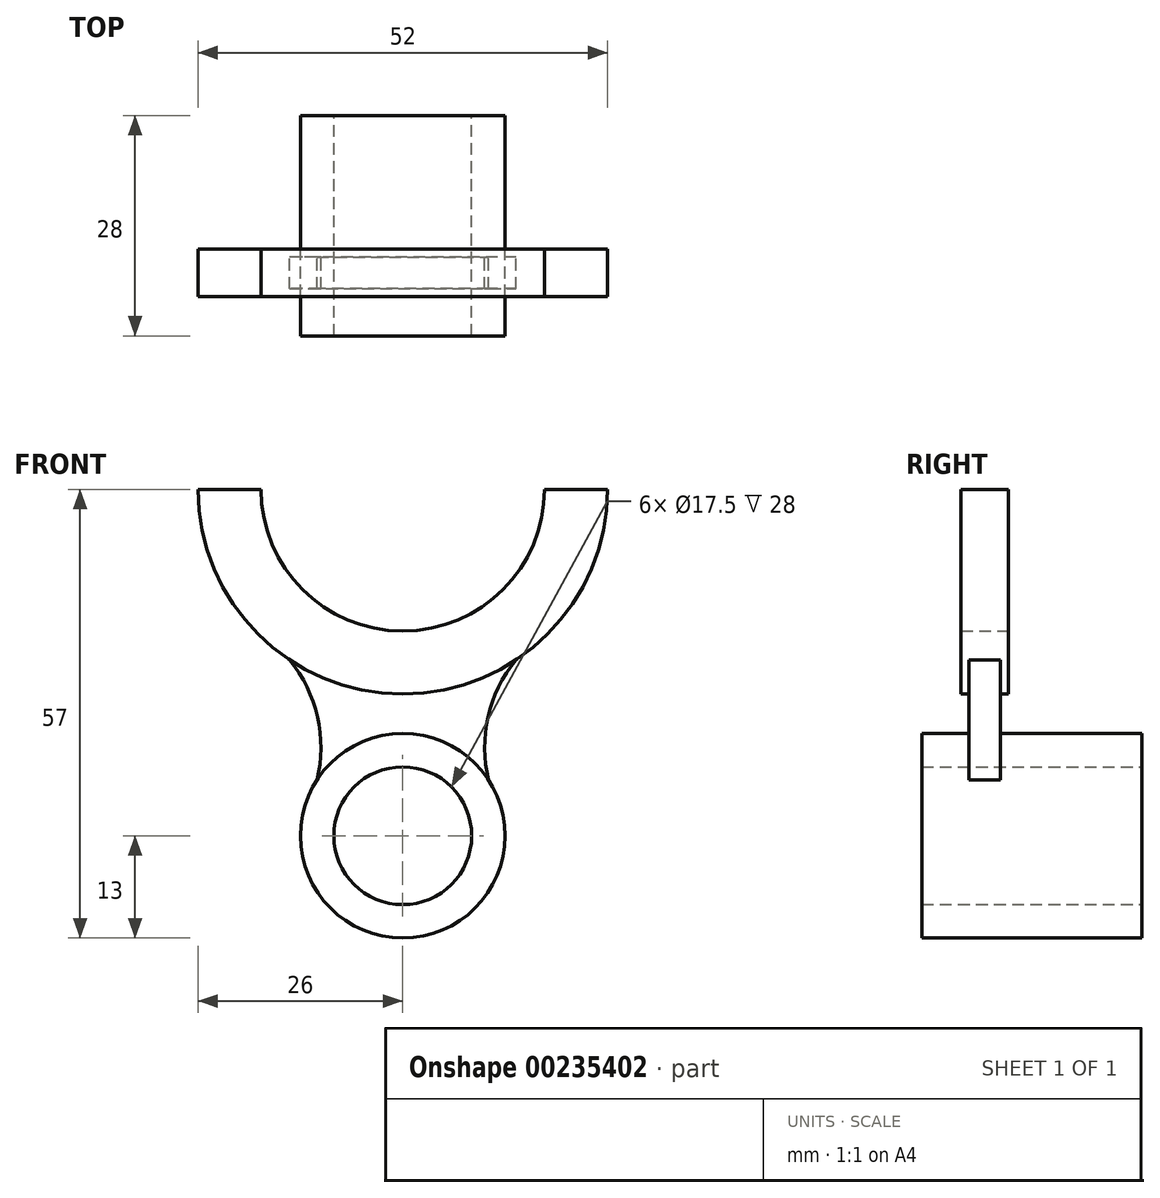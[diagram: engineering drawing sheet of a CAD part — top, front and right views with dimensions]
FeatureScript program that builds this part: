
annotation { "Feature Type Name" : "Feature", "Feature Type Description" : "" }
export const myFeature = defineFeature(function(context is Context, id is Id, definition is map)
    precondition{}
    {
        {
            var Q0;
            Q0=qCreatedBy(makeId("Front.planeOp"),FACE);
            var sketch = newSketch(context, id + "F0", { "sketchPlane" : qUnion([Q0])});
            skCircle(sketch, "E0", {"center": v(0, 0) * mm, "radius": 8.75 * mm});
            skCircle(sketch, "E1", {"center": v(0, 0) * mm, "radius": 13 * mm});
            skArc(sketch, "E2", {"start": v(12.76, 2.47) * mm, "mid": v(10.99, 15.74) * mm, "end": v(19.12, 26.38) * mm});
            skArc(sketch, "E3.MirrorCS", {"start": v(-12.76, 2.47) * mm, "mid": v(-10.99, 15.74) * mm, "end": v(-19.12, 26.38) * mm});
            skArc(sketch, "E4", {"start": v(-26, 44) * mm, "mid": v(0, 18) * mm, "end": v(26, 44) * mm});
            skLineSegment(sketch, "E5", {"start": v(-26, 44) * mm, "end": v(-18, 44) * mm});
            skArc(sketch, "E6", {"start": v(-18, 44) * mm, "mid": v(0, 26) * mm, "end": v(18, 44) * mm});
            skLineSegment(sketch, "E7", {"start": v(18, 44) * mm, "end": v(26, 44) * mm});
            skSolve(sketch);
        }
        {
            var Q0;
            Q0 = qSketchRegion(id + "F0", true);
            extrude(context, id + "F1", {"entities" : qUnion([Q0]), "depth" : 28 * mm});
        }
        {
            var Q0;
            Q0=makeQuery(id+"F1.opExtrude","CAP_FACE",FACE,{"disambiguationData":[OSD([sQuery(id+"F0.wireOp",EDGE,"E2"),sQuery(id+"F0.wireOp",EDGE,"E3.MirrorCS"),sQuery(id+"F0.wireOp",EDGE,"E1"),sQuery(id+"F0.wireOp",EDGE,"E0"),sQuery(id+"F0.wireOp",EDGE,"E4"),sQuery(id+"F0.wireOp",EDGE,"E5"),sQuery(id+"F0.wireOp",EDGE,"E6"),sQuery(id+"F0.wireOp",EDGE,"E7")])],"isStart":false});
            var sketch = newSketch(context, id + "F2", { "sketchPlane" : qUnion([Q0])});
            skLineSegment(sketch, "E8", {"start": v(-26, 44) * mm, "end": v(-18, 44) * mm});
            skArc(sketch, "E9", {"start": v(-18, 44) * mm, "mid": v(0, 26) * mm, "end": v(18, 44) * mm});
            skLineSegment(sketch, "E10", {"start": v(18, 44) * mm, "end": v(26, 44) * mm});
            skArc(sketch, "E11", {"start": v(26, 44) * mm, "mid": v(22.9, 31.7) * mm, "end": v(14.35, 22.32) * mm});
            skArc(sketch, "E12", {"start": v(-26, 44) * mm, "mid": v(-22.9, 31.7) * mm, "end": v(-14.35, 22.32) * mm});
            skArc(sketch, "E13", {"start": v(-14.35, 22.32) * mm, "mid": v(-10.83, 15.1) * mm, "end": v(-10.9, 7.07) * mm});
            skArc(sketch, "E14", {"start": v(14.35, 22.32) * mm, "mid": v(10.83, 15.1) * mm, "end": v(10.9, 7.07) * mm});
            skArc(sketch, "E15", {"start": v(-10.9, 7.07) * mm, "mid": v(0, 13) * mm, "end": v(10.9, 7.07) * mm});
            skSolve(sketch);
        }
        {
            var Q0;
            Q0 = qSketchRegion(id + "F2", true);
            extrude(context, id + "F3", {"entities" : qUnion([Q0]), "operationType" : NewBodyOperationType.REMOVE, "oppositeDirection" : true, "depth" : 5 * mm});
        }
        {
            var Q0;
            Q0=makeQuery(id+"F1.opExtrude","CAP_FACE",FACE,{"disambiguationData":[OSD([sQuery(id+"F0.wireOp",EDGE,"E2"),sQuery(id+"F0.wireOp",EDGE,"E3.MirrorCS"),sQuery(id+"F0.wireOp",EDGE,"E1"),sQuery(id+"F0.wireOp",EDGE,"E0"),sQuery(id+"F0.wireOp",EDGE,"E4"),sQuery(id+"F0.wireOp",EDGE,"E5"),sQuery(id+"F0.wireOp",EDGE,"E6"),sQuery(id+"F0.wireOp",EDGE,"E7")])],"isStart":true});
            var sketch = newSketch(context, id + "F4", { "sketchPlane" : qUnion([Q0])});
            skLineSegment(sketch, "E16", {"start": v(-26, 44) * mm, "end": v(-18, 44) * mm});
            skArc(sketch, "E17", {"start": v(18, 44) * mm, "mid": v(0, 26) * mm, "end": v(-18, 44) * mm});
            skLineSegment(sketch, "E18", {"start": v(18, 44) * mm, "end": v(26, 44) * mm});
            skArc(sketch, "E19", {"start": v(26, 44) * mm, "mid": v(22.9, 31.7) * mm, "end": v(14.35, 22.32) * mm});
            skArc(sketch, "E20", {"start": v(-26, 44) * mm, "mid": v(-22.9, 31.7) * mm, "end": v(-14.35, 22.32) * mm});
            skArc(sketch, "E21", {"start": v(-10.9, 7.07) * mm, "mid": v(0, 13) * mm, "end": v(10.9, 7.07) * mm});
            skArc(sketch, "E22", {"start": v(-14.35, 22.32) * mm, "mid": v(-10.83, 15.1) * mm, "end": v(-10.9, 7.07) * mm});
            skArc(sketch, "E23", {"start": v(14.35, 22.32) * mm, "mid": v(10.83, 15.1) * mm, "end": v(10.9, 7.07) * mm});
            skSolve(sketch);
        }
        {
            var Q0;
            Q0=makeQuery(id+"F4.imprint","IMPRINT",FACE,{"disambiguationData":[TD([[makeQuery(id+"F4.imprint","IMPRINT",EDGE,{"derivedFrom":sQuery(id+"F4.wireOp",EDGE,"E16")}),1.0]])]});
            extrude(context, id + "F5", {"entities" : qUnion([Q0]), "operationType" : NewBodyOperationType.REMOVE, "oppositeDirection" : true, "depth" : 17 * mm});
        }
        {
            var Q0;
            Q0=makeQuery(id+"F3.boolean.opBoolean","COPY",FACE,{"derivedFrom":makeQuery(id+"F3.opExtrude","CAP_FACE",FACE,{"disambiguationData":[OSD([sQuery(id+"F2.wireOp",EDGE,"E8"),sQuery(id+"F2.wireOp",EDGE,"E9"),sQuery(id+"F2.wireOp",EDGE,"E10"),sQuery(id+"F2.wireOp",EDGE,"E11"),sQuery(id+"F2.wireOp",EDGE,"E12"),sQuery(id+"F2.wireOp",EDGE,"E13"),sQuery(id+"F2.wireOp",EDGE,"E14"),sQuery(id+"F2.wireOp",EDGE,"E15")])],"isStart":false})});
            var sketch = newSketch(context, id + "F6", { "sketchPlane" : qUnion([Q0])});
            skArc(sketch, "E24", {"start": v(-14.35, 22.32) * mm, "mid": v(0, 18) * mm, "end": v(14.35, 22.32) * mm});
            skArc(sketch, "E25", {"start": v(-14.35, 22.32) * mm, "mid": v(-10.83, 15.1) * mm, "end": v(-10.9, 7.07) * mm});
            skArc(sketch, "E26", {"start": v(-10.9, 7.07) * mm, "mid": v(0, 13) * mm, "end": v(10.9, 7.07) * mm});
            skArc(sketch, "E27", {"start": v(14.35, 22.32) * mm, "mid": v(10.83, 15.1) * mm, "end": v(10.9, 7.07) * mm});
            skSolve(sketch);
        }
        {
            var Q0;
            Q0 = qSketchRegion(id + "F6", true);
            extrude(context, id + "F7", {"entities" : qUnion([Q0]), "operationType" : NewBodyOperationType.REMOVE, "oppositeDirection" : true, "depth" : 1 * mm});
        }
        {
            var Q0;
            Q0=makeQuery(id+"F5.boolean.opBoolean","COPY",FACE,{"derivedFrom":makeQuery(id+"F5.opExtrude","CAP_FACE",FACE,{"disambiguationData":[OSD([sQuery(id+"F4.wireOp",EDGE,"E16"),sQuery(id+"F4.wireOp",EDGE,"E17"),sQuery(id+"F4.wireOp",EDGE,"E18"),sQuery(id+"F4.wireOp",EDGE,"E19"),sQuery(id+"F4.wireOp",EDGE,"E20"),sQuery(id+"F4.wireOp",EDGE,"E21"),sQuery(id+"F4.wireOp",EDGE,"E22"),sQuery(id+"F4.wireOp",EDGE,"E23")])],"isStart":false})});
            var sketch = newSketch(context, id + "F8", { "sketchPlane" : qUnion([Q0])});
            skArc(sketch, "E28", {"start": v(-14.35, 22.32) * mm, "mid": v(-10.83, 15.1) * mm, "end": v(-10.9, 7.07) * mm});
            skArc(sketch, "E29", {"start": v(-10.9, 7.07) * mm, "mid": v(0, 13) * mm, "end": v(10.9, 7.07) * mm});
            skArc(sketch, "E30", {"start": v(14.35, 22.32) * mm, "mid": v(10.83, 15.1) * mm, "end": v(10.9, 7.07) * mm});
            skArc(sketch, "E31", {"start": v(14.35, 22.32) * mm, "mid": v(0, 18) * mm, "end": v(-14.35, 22.32) * mm});
            skSolve(sketch);
        }
        {
            var Q0;
            Q0 = qSketchRegion(id + "F8", true);
            extrude(context, id + "F9", {"entities" : qUnion([Q0]), "operationType" : NewBodyOperationType.REMOVE, "oppositeDirection" : true, "depth" : 1 * mm});
        }
    });
